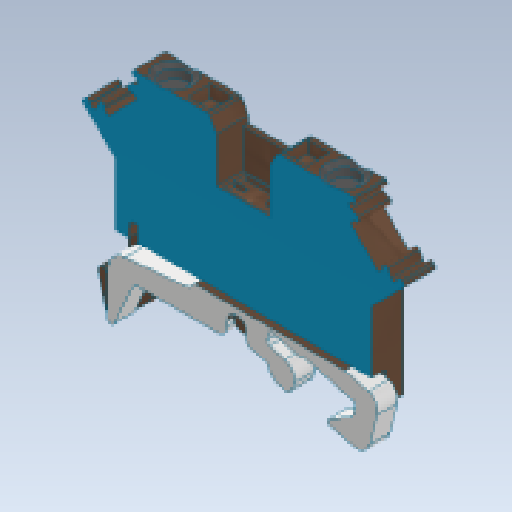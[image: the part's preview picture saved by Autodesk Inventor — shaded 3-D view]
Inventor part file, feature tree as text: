
AUTODESK INVENTOR PART (.ipt)
format: ipt  version: 2025.2 (Build 292293000, 293)  size: 824,320 bytes
history: native  units: mm
features: other x130, sketch x12, extrude x10, hole x2
ambient origin geometry x8: Origin, YZ Plane, XZ Plane, XY Plane, X Axis, Y Axis, Z Axis, Center Point
bodies: Solid1 (feature_tree)
feature tree (154):
  extrude  "Extrusion1"  Depth=2.1mm TaperAngle=0.0deg
  extrude  "Extrusion2"  Depth=2.0mm TaperAngle=0.0deg
  extrude  "Extrusion3"  Depth=7.0mm TaperAngle=0.0deg
  extrude  "Extrusion4"  Depth=5.0mm TaperAngle=0.0deg
  extrude  "Extrusion5"  Depth=3.6mm TaperAngle=0.0deg
  extrude  "Extrusion6"  TaperAngle=0.0deg  [1 undecoded]
  extrude  "Extrusion7"  TaperAngle=0.0deg  [1 undecoded]
  extrude  "Extrusion8"  TaperAngle=0.0deg  [1 undecoded]
  hole  "Hole1"  [1 undecoded]
  hole  "Hole2"  [1 undecoded]
  extrude  "Extrusion9"  Depth=10.0mm
  extrude  "Extrusion10"  Depth=10.0mm
  other  "1_2_XY"
  other  "1_2_YZ"
  other  "1_2_ZX"
  other  "1_2_X"
  other  "1_2_Y"
  other  "1_2_Z"
  other  "1_2_Center"
  other  "1_3_XY"
  other  "1_3_YZ"
  other  "1_3_ZX"
  other  "1_3_X"
  other  "1_3_Y"
  other  "1_3_Z"
  other  "1_3_Center"
  other  "1_4_XY"
  other  "1_4_YZ"
  other  "1_4_ZX"
  other  "1_4_X"
  other  "1_4_Y"
  other  "1_4_Z"
  other  "1_4_Center"
  other  "1_5_XY"
  other  "1_5_YZ"
  other  "1_5_ZX"
  other  "1_5_X"
  other  "1_5_Y"
  other  "1_5_Z"
  other  "1_5_Center"
  other  "1_6_XY"
  other  "1_6_YZ"
  other  "1_6_ZX"
  other  "1_6_X"
  other  "1_6_Y"
  other  "1_6_Z"
  other  "1_6_Center"
  other  "1_7_XY"
  other  "1_7_YZ"
  other  "1_7_ZX"
  other  "1_7_X"
  other  "1_7_Y"
  other  "1_7_Z"
  other  "1_7_Center"
  other  "1_8_XY"
  other  "1_8_YZ"
  other  "1_8_ZX"
  other  "1_8_X"
  other  "1_8_Y"
  other  "1_8_Z"
  other  "1_8_Center"
  other  "MD_XY"
  other  "MD_YZ"
  other  "MD_ZX"
  other  "MD_X"
  other  "MD_Y"
  other  "MD_Z"
  other  "MD_Center"
  other  "OP_XY"
  other  "OP_YZ"
  other  "OP_ZX"
  other  "OP_X"
  other  "OP_Y"
  other  "OP_Z"
  other  "OP_Center"
  other  "a1_XY"
  other  "a1_YZ"
  other  "a1_ZX"
  other  "a1_X"
  other  "a1_Y"
  other  "a1_Z"
  other  "a1_Center"
  other  "b2_XY"
  other  "b2_YZ"
  other  "b2_ZX"
  other  "b2_X"
  other  "b2_Y"
  other  "b2_Z"
  other  "b2_Center"
  other  "j3_XY"
  other  "j3_YZ"
  other  "j3_ZX"
  other  "j3_X"
  other  "j3_Y"
  other  "j3_Z"
  other  "j3_Center"
  other  "m4_XY"
  other  "m4_YZ"
  other  "m4_ZX"
  other  "m4_X"
  other  "m4_Y"
  other  "m4_Z"
  other  "m4_Center"
  other  "m5_XY"
  other  "m5_YZ"
  other  "m5_ZX"
  other  "m5_X"
  other  "m5_Y"
  other  "m5_Z"
  other  "m5_Center"
  other  "z6_XY"
  other  "z6_YZ"
  other  "z6_ZX"
  other  "z6_X"
  other  "z6_Y"
  other  "z6_Z"
  other  "z6_Center"
  other  "z7_XY"
  other  "z7_YZ"
  other  "z7_ZX"
  other  "z7_X"
  other  "z7_Y"
  other  "z7_Z"
  other  "z7_Center"
  other  "Edição direta1"
  other  "Edição direta2"
  other  "Edição direta3"
  other  "Edição direta4"
  other  "Edição direta5"
  other  "Edição direta6"
  other  "Edição direta7"
  other  "Edição direta8"
  other  "Edição direta9"
  sketch  "Skizze_1"  dims[d0=5.0mm d1=0.0mm d2=2.1mm d3=0.0mm]
  sketch  "Skizze_14"  dims[d39=0.0mm d40=0.0mm]
  sketch  "Skizze_15"  dims[d41=3.0mm d42=10.0mm d43=10.0mm d44=12.3mm d45=10.0mm d46=10.0mm]
  sketch  "Skizze_16"  dims[d47=12.0mm d48=10.0mm d49=10.0mm d50=0.25mm d51=0.55mm d52=-0.36mm d53=-0.4mm d54=0.0mm d55=0.0mm d56=0.0mm d57=0.0mm d58=0.35mm d59=0.5mm]
  sketch  "Skizze_2"  dims[d4=2.1mm d5=0.0mm d6=2.0mm d7=0.0mm]
  sketch  "Skizze_3"  dims[d8=0.8mm d9=0.0mm d10=7.0mm d11=0.0mm]
  sketch  "Skizze_4"  dims[d12=3.4mm d13=0.0mm d14=5.0mm d15=0.0mm]
  sketch  "Skizze_5"  dims[d16=4.2mm d17=6.0mm d18=5.8mm d19=2.0mm d20=18.545904mm d21=2.0mm d22=0.0mm]
  sketch  "Sketch9"  dims[d32=3.6mm d33=0.0mm d34=0.0mm]
  sketch  "Sketch10"  dims[d37=0.0mm d38=0.0mm]
  sketch  "Skizze_8"  dims[d23=4.2mm d24=6.0mm d25=5.8mm d26=2.0mm d27=18.545904mm d28=2.0mm d29=0.0mm d30=3.6mm d31=0.0mm]
  sketch  "Skizze_9"  dims[d35=0.0mm d36=0.0mm]
  other  "Escala1"
  other  "Escala2"
  other  "Escala3"
  other  "Tamanho1"
  other  "Tamanho2"
  other  "Tamanho3"
  other  "Mover1"
  other  "Mover2"
  other  "Tamanho4"
note: 5 required parameter values undecoded (feature->parameter linkage not recoverable at this tier; creation-order binding heuristic only, values carry confidence <= 0.55)
